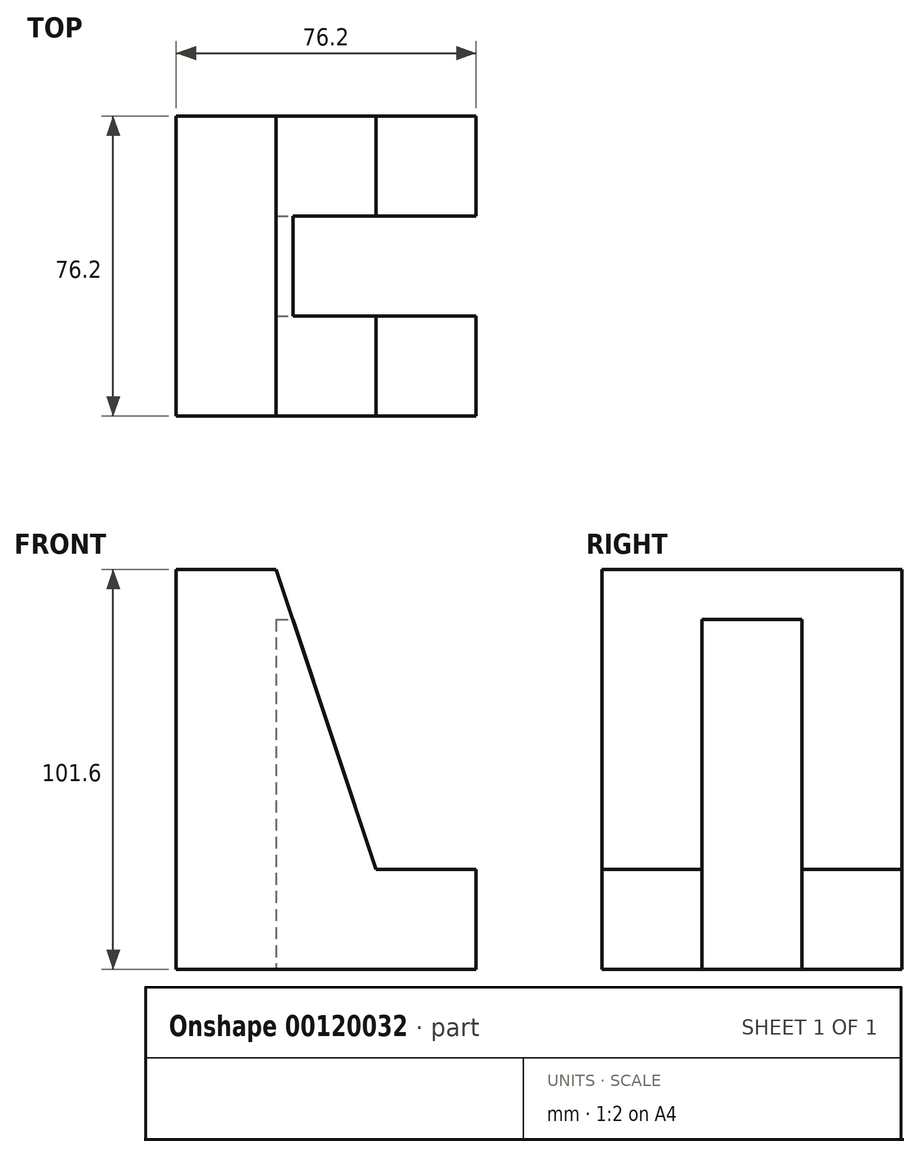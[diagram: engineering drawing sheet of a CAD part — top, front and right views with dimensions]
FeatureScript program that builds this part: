
annotation { "Feature Type Name" : "Feature", "Feature Type Description" : "" }
export const myFeature = defineFeature(function(context is Context, id is Id, definition is map)
    precondition{}
    {
        {
            var Q0;
            Q0=qCreatedBy(makeId("Front.planeOp"),FACE);
            var sketch = newSketch(context, id + "F0", { "sketchPlane" : qUnion([Q0])});
            skLineSegment(sketch, "E0", {"start": v(0, 101.6) * mm, "end": v(25.4, 101.6) * mm});
            skLineSegment(sketch, "E1", {"start": v(25.4, 101.6) * mm, "end": v(50.8, 25.4) * mm});
            skLineSegment(sketch, "E2", {"start": v(50.8, 25.4) * mm, "end": v(76.2, 25.4) * mm});
            skLineSegment(sketch, "E3", {"start": v(76.2, 25.4) * mm, "end": v(76.2, 0) * mm});
            skLineSegment(sketch, "E4", {"start": v(76.2, 0) * mm, "end": v(0, 0) * mm});
            skLineSegment(sketch, "E5", {"start": v(0, 0) * mm, "end": v(0, 101.6) * mm});
            skSolve(sketch);
        }
        {
            var Q0;
            Q0 = qSketchRegion(id + "F0", true);
            extrude(context, id + "F1", {"entities" : qUnion([Q0]), "depth" : 76.2 * mm});
        }
        {
            var Q0;
            Q0=qCreatedBy(makeId("Top.planeOp"),FACE);
            var sketch = newSketch(context, id + "F2", { "sketchPlane" : qUnion([Q0])});
            skLineSegment(sketch, "E6.bottom", {"start": v(25.4, -25.4) * mm, "end": v(76.2, -25.4) * mm});
            skLineSegment(sketch, "E6.top", {"start": v(25.4, -50.8) * mm, "end": v(76.2, -50.8) * mm});
            skLineSegment(sketch, "E6.left", {"start": v(25.4, -25.4) * mm, "end": v(25.4, -50.8) * mm});
            skLineSegment(sketch, "E6.right", {"start": v(76.2, -25.4) * mm, "end": v(76.2, -50.8) * mm});
            skSolve(sketch);
        }
        {
            var Q0;
            Q0 = qSketchRegion(id + "F2", true);
            extrude(context, id + "F3", {"entities" : qUnion([Q0]), "operationType" : NewBodyOperationType.REMOVE, "depth" : 88.9 * mm});
        }
    });
